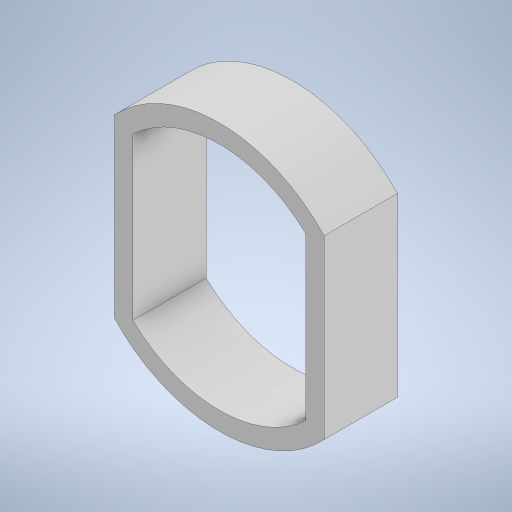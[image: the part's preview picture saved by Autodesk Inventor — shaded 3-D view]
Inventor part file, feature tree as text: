
AUTODESK INVENTOR PART (.ipt)
format: ipt  version: 2024 (Build 280153000, 153)  size: 232,960 bytes
history: native  units: in
note: dims shown in document units (in); Inventor stores cm internally (conversion verified against a paired STEP export)
features: extrude x1, sketch x1
ambient origin geometry x8: Origin, YZ Plane, XZ Plane, XY Plane, X Axis, Y Axis, Z Axis, Center Point
bodies: Solid1 (feature_tree)
feature tree (2):
  extrude  "Extrusion1"  Depth=0.25in
  sketch  "Sketch1"  dims[d2=0.5906in d3=0.7874in d4=0.5512in d5=0.2953in d6=0.3937in d7=0.0625in d8=0.0625in d9=0.25in d10=0.0in]
